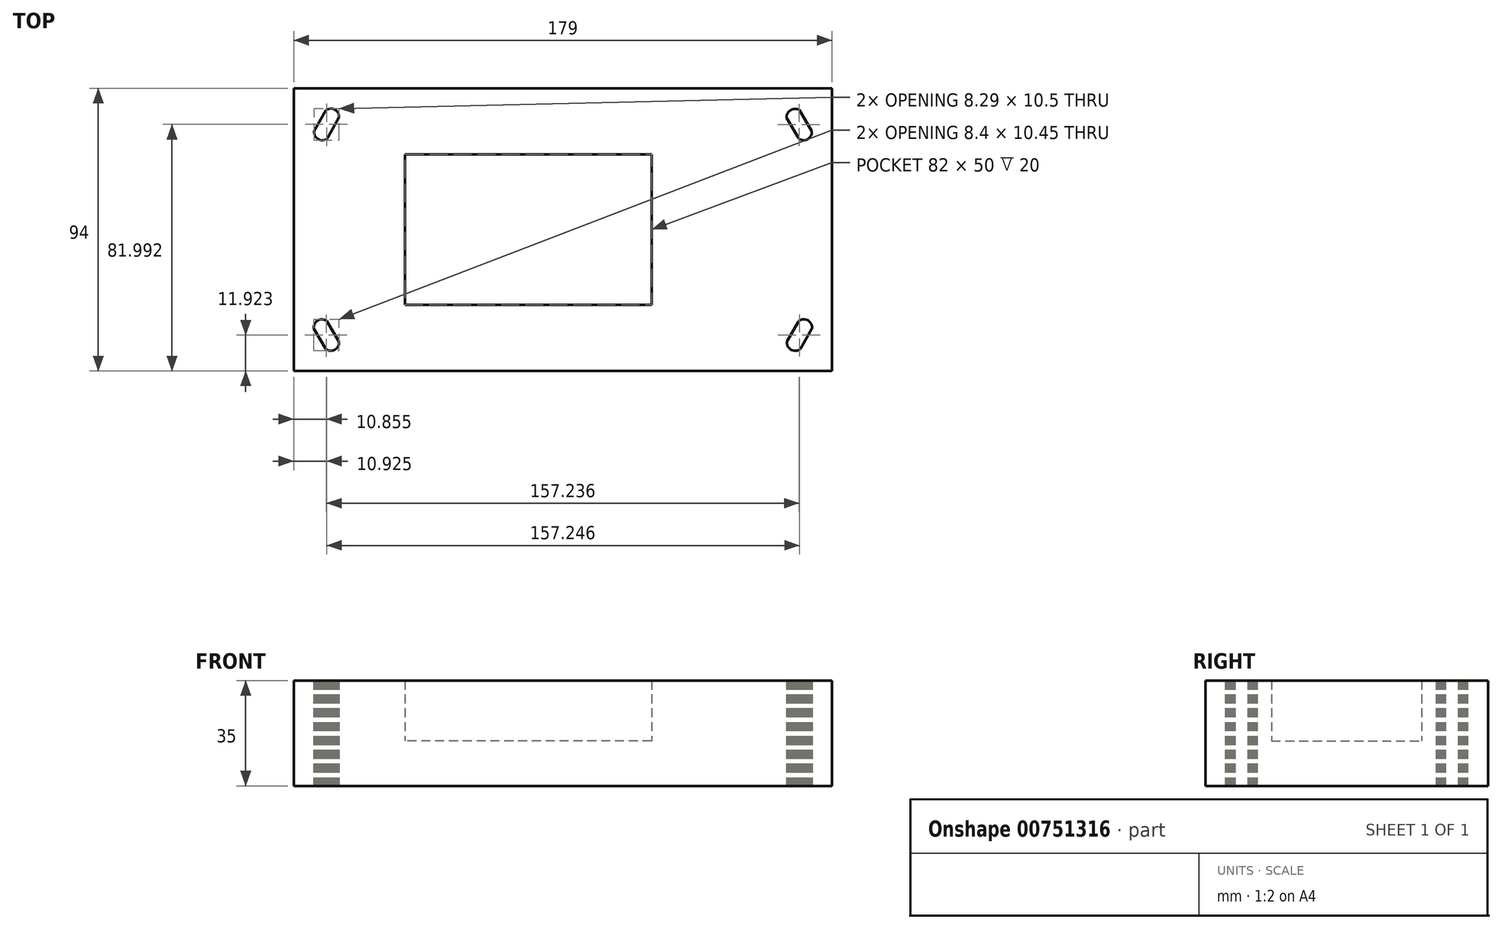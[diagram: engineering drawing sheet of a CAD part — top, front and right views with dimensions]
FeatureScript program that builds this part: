
annotation { "Feature Type Name" : "Feature", "Feature Type Description" : "" }
export const myFeature = defineFeature(function(context is Context, id is Id, definition is map)
    precondition{}
    {
        {
            var Q0;
            Q0=qCreatedBy(makeId("Top.planeOp"),FACE);
            var sketch = newSketch(context, id + "F0", { "sketchPlane" : qUnion([Q0])});
            skLineSegment(sketch, "E0", {"start": v(-79, -30.08) * mm, "end": v(-78.54, -30.33) * mm});
            skLineSegment(sketch, "E1", {"start": v(-79.49, -29.92) * mm, "end": v(-79, -30.08) * mm});
            skLineSegment(sketch, "E2", {"start": v(-80, -29.85) * mm, "end": v(-79.49, -29.92) * mm});
            skLineSegment(sketch, "E3", {"start": v(-80.53, -29.89) * mm, "end": v(-80, -29.85) * mm});
            skLineSegment(sketch, "E4", {"start": v(-81.03, -30.02) * mm, "end": v(-80.53, -29.89) * mm});
            skLineSegment(sketch, "E5", {"start": v(-81.5, -30.24) * mm, "end": v(-81.03, -30.02) * mm});
            skLineSegment(sketch, "E6", {"start": v(-81.92, -30.54) * mm, "end": v(-81.5, -30.24) * mm});
            skLineSegment(sketch, "E7", {"start": v(-82.28, -30.92) * mm, "end": v(-81.92, -30.54) * mm});
            skLineSegment(sketch, "E8", {"start": v(-82.56, -31.36) * mm, "end": v(-82.28, -30.92) * mm});
            skLineSegment(sketch, "E9", {"start": v(-82.75, -31.85) * mm, "end": v(-82.56, -31.36) * mm});
            skLineSegment(sketch, "E10", {"start": v(-82.84, -32.36) * mm, "end": v(-82.75, -31.85) * mm});
            skLineSegment(sketch, "E11", {"start": v(-82.84, -32.88) * mm, "end": v(-82.84, -32.36) * mm});
            skLineSegment(sketch, "E12", {"start": v(-78.77, -39.77) * mm, "end": v(-82.84, -32.88) * mm});
            skLineSegment(sketch, "E13", {"start": v(-78.32, -40.04) * mm, "end": v(-78.77, -39.77) * mm});
            skLineSegment(sketch, "E14", {"start": v(-77.82, -40.22) * mm, "end": v(-78.32, -40.04) * mm});
            skLineSegment(sketch, "E15", {"start": v(-77.3, -40.3) * mm, "end": v(-77.82, -40.22) * mm});
            skLineSegment(sketch, "E16", {"start": v(-76.77, -40.28) * mm, "end": v(-77.3, -40.3) * mm});
            skLineSegment(sketch, "E17", {"start": v(-76.25, -40.15) * mm, "end": v(-76.77, -40.28) * mm});
            skLineSegment(sketch, "E18", {"start": v(-75.77, -39.93) * mm, "end": v(-76.25, -40.15) * mm});
            skLineSegment(sketch, "E19", {"start": v(-75.34, -39.61) * mm, "end": v(-75.77, -39.93) * mm});
            skLineSegment(sketch, "E20", {"start": v(-74.99, -39.22) * mm, "end": v(-75.34, -39.61) * mm});
            skLineSegment(sketch, "E21", {"start": v(-74.71, -38.77) * mm, "end": v(-74.99, -39.22) * mm});
            skLineSegment(sketch, "E22", {"start": v(-74.53, -38.27) * mm, "end": v(-74.71, -38.77) * mm});
            skLineSegment(sketch, "E23", {"start": v(-74.45, -37.75) * mm, "end": v(-74.53, -38.27) * mm});
            skLineSegment(sketch, "E24", {"start": v(78.7, 39.7) * mm, "end": v(82.77, 32.8) * mm});
            skLineSegment(sketch, "E25", {"start": v(78.24, 39.94) * mm, "end": v(78.7, 39.7) * mm});
            skLineSegment(sketch, "E26", {"start": v(77.75, 40.1) * mm, "end": v(78.24, 39.94) * mm});
            skLineSegment(sketch, "E27", {"start": v(77.23, 40.17) * mm, "end": v(77.75, 40.1) * mm});
            skLineSegment(sketch, "E28", {"start": v(76.7, 40.14) * mm, "end": v(77.23, 40.17) * mm});
            skLineSegment(sketch, "E29", {"start": v(76.2, 40) * mm, "end": v(76.7, 40.14) * mm});
            skLineSegment(sketch, "E30", {"start": v(75.73, 39.79) * mm, "end": v(76.2, 40) * mm});
            skLineSegment(sketch, "E31", {"start": v(75.31, 39.48) * mm, "end": v(75.73, 39.79) * mm});
            skLineSegment(sketch, "E32", {"start": v(74.96, 39.1) * mm, "end": v(75.31, 39.48) * mm});
            skLineSegment(sketch, "E33", {"start": v(74.68, 38.66) * mm, "end": v(74.96, 39.1) * mm});
            skLineSegment(sketch, "E34", {"start": v(74.49, 38.18) * mm, "end": v(74.68, 38.66) * mm});
            skLineSegment(sketch, "E35", {"start": v(74.4, 37.67) * mm, "end": v(74.49, 38.18) * mm});
            skLineSegment(sketch, "E36", {"start": v(78.92, 29.99) * mm, "end": v(78.47, 30.26) * mm});
            skLineSegment(sketch, "E37", {"start": v(79.42, 29.8) * mm, "end": v(78.92, 29.99) * mm});
            skLineSegment(sketch, "E38", {"start": v(79.94, 29.73) * mm, "end": v(79.42, 29.8) * mm});
            skLineSegment(sketch, "E39", {"start": v(80.47, 29.75) * mm, "end": v(79.94, 29.73) * mm});
            skLineSegment(sketch, "E40", {"start": v(80.98, 29.88) * mm, "end": v(80.47, 29.75) * mm});
            skLineSegment(sketch, "E41", {"start": v(81.46, 30.1) * mm, "end": v(80.98, 29.88) * mm});
            skLineSegment(sketch, "E42", {"start": v(81.9, 30.41) * mm, "end": v(81.46, 30.1) * mm});
            skLineSegment(sketch, "E43", {"start": v(82.25, 30.8) * mm, "end": v(81.9, 30.41) * mm});
            skLineSegment(sketch, "E44", {"start": v(82.53, 31.25) * mm, "end": v(82.25, 30.8) * mm});
            skLineSegment(sketch, "E45", {"start": v(82.7, 31.75) * mm, "end": v(82.53, 31.25) * mm});
            skLineSegment(sketch, "E46", {"start": v(82.8, 32.28) * mm, "end": v(82.7, 31.75) * mm});
            skLineSegment(sketch, "E47", {"start": v(82.77, 32.8) * mm, "end": v(82.8, 32.28) * mm});
            skLineSegment(sketch, "E48", {"start": v(-74.54, 38.3) * mm, "end": v(-74.44, 37.8) * mm});
            skLineSegment(sketch, "E49", {"start": v(-74.75, 38.79) * mm, "end": v(-74.54, 38.3) * mm});
            skLineSegment(sketch, "E50", {"start": v(-75.03, 39.22) * mm, "end": v(-74.75, 38.79) * mm});
            skLineSegment(sketch, "E51", {"start": v(-75.4, 39.6) * mm, "end": v(-75.03, 39.22) * mm});
            skLineSegment(sketch, "E52", {"start": v(-75.82, 39.9) * mm, "end": v(-75.4, 39.6) * mm});
            skLineSegment(sketch, "E53", {"start": v(-76.3, 40.1) * mm, "end": v(-75.82, 39.9) * mm});
            skLineSegment(sketch, "E54", {"start": v(-76.8, 40.22) * mm, "end": v(-76.3, 40.1) * mm});
            skLineSegment(sketch, "E55", {"start": v(-77.33, 40.24) * mm, "end": v(-76.8, 40.22) * mm});
            skLineSegment(sketch, "E56", {"start": v(-77.84, 40.16) * mm, "end": v(-77.33, 40.24) * mm});
            skLineSegment(sketch, "E57", {"start": v(-78.33, 40) * mm, "end": v(-77.84, 40.16) * mm});
            skLineSegment(sketch, "E58", {"start": v(-78.78, 39.73) * mm, "end": v(-78.33, 40) * mm});
            skLineSegment(sketch, "E59", {"start": v(-82.71, 32.76) * mm, "end": v(-78.78, 39.73) * mm});
            skLineSegment(sketch, "E60", {"start": v(-82.72, 32.23) * mm, "end": v(-82.71, 32.76) * mm});
            skLineSegment(sketch, "E61", {"start": v(-82.63, 31.7) * mm, "end": v(-82.72, 32.23) * mm});
            skLineSegment(sketch, "E62", {"start": v(-82.44, 31.22) * mm, "end": v(-82.63, 31.7) * mm});
            skLineSegment(sketch, "E63", {"start": v(-82.15, 30.77) * mm, "end": v(-82.44, 31.22) * mm});
            skLineSegment(sketch, "E64", {"start": v(-81.78, 30.39) * mm, "end": v(-82.15, 30.77) * mm});
            skLineSegment(sketch, "E65", {"start": v(-81.35, 30.08) * mm, "end": v(-81.78, 30.39) * mm});
            skLineSegment(sketch, "E66", {"start": v(-80.87, 29.87) * mm, "end": v(-81.35, 30.08) * mm});
            skLineSegment(sketch, "E67", {"start": v(-80.35, 29.75) * mm, "end": v(-80.87, 29.87) * mm});
            skLineSegment(sketch, "E68", {"start": v(-79.82, 29.74) * mm, "end": v(-80.35, 29.75) * mm});
            skLineSegment(sketch, "E69", {"start": v(-79.3, 29.83) * mm, "end": v(-79.82, 29.74) * mm});
            skLineSegment(sketch, "E70", {"start": v(-78.8, 30.02) * mm, "end": v(-79.3, 29.83) * mm});
            skLineSegment(sketch, "E71", {"start": v(-78.36, 30.3) * mm, "end": v(-78.8, 30.02) * mm});
            skLineSegment(sketch, "E72", {"start": v(82.82, -32.76) * mm, "end": v(78.9, -39.73) * mm});
            skLineSegment(sketch, "E73", {"start": v(82.8, -32.24) * mm, "end": v(82.82, -32.76) * mm});
            skLineSegment(sketch, "E74", {"start": v(82.7, -31.73) * mm, "end": v(82.8, -32.24) * mm});
            skLineSegment(sketch, "E75", {"start": v(82.5, -31.25) * mm, "end": v(82.7, -31.73) * mm});
            skLineSegment(sketch, "E76", {"start": v(82.21, -30.82) * mm, "end": v(82.5, -31.25) * mm});
            skLineSegment(sketch, "E77", {"start": v(81.85, -30.45) * mm, "end": v(82.21, -30.82) * mm});
            skLineSegment(sketch, "E78", {"start": v(81.42, -30.15) * mm, "end": v(81.85, -30.45) * mm});
            skLineSegment(sketch, "E79", {"start": v(80.95, -29.94) * mm, "end": v(81.42, -30.15) * mm});
            skLineSegment(sketch, "E80", {"start": v(80.44, -29.82) * mm, "end": v(80.95, -29.94) * mm});
            skLineSegment(sketch, "E81", {"start": v(79.92, -29.8) * mm, "end": v(80.44, -29.82) * mm});
            skLineSegment(sketch, "E82", {"start": v(79.4, -29.88) * mm, "end": v(79.92, -29.8) * mm});
            skLineSegment(sketch, "E83", {"start": v(78.91, -30.05) * mm, "end": v(79.4, -29.88) * mm});
            skLineSegment(sketch, "E84", {"start": v(78.46, -30.3) * mm, "end": v(78.91, -30.05) * mm});
            skLineSegment(sketch, "E85", {"start": v(74.62, -38.33) * mm, "end": v(74.52, -37.8) * mm});
            skLineSegment(sketch, "E86", {"start": v(74.81, -38.82) * mm, "end": v(74.62, -38.33) * mm});
            skLineSegment(sketch, "E87", {"start": v(75.1, -39.27) * mm, "end": v(74.81, -38.82) * mm});
            skLineSegment(sketch, "E88", {"start": v(75.46, -39.65) * mm, "end": v(75.1, -39.27) * mm});
            skLineSegment(sketch, "E89", {"start": v(75.9, -39.96) * mm, "end": v(75.46, -39.65) * mm});
            skLineSegment(sketch, "E90", {"start": v(76.38, -40.17) * mm, "end": v(75.9, -39.96) * mm});
            skLineSegment(sketch, "E91", {"start": v(76.9, -40.29) * mm, "end": v(76.38, -40.17) * mm});
            skLineSegment(sketch, "E92", {"start": v(77.43, -40.3) * mm, "end": v(76.9, -40.29) * mm});
            skLineSegment(sketch, "E93", {"start": v(77.95, -40.2) * mm, "end": v(77.43, -40.3) * mm});
            skLineSegment(sketch, "E94", {"start": v(78.44, -40.02) * mm, "end": v(77.95, -40.2) * mm});
            skLineSegment(sketch, "E95", {"start": v(78.9, -39.73) * mm, "end": v(78.44, -40.02) * mm});
            skLineSegment(sketch, "E96", {"start": v(92.5, -50) * mm, "end": v(-92.5, -50) * mm});
            skLineSegment(sketch, "E97", {"start": v(-92.5, -50) * mm, "end": v(-92.5, 50) * mm});
            skLineSegment(sketch, "E98", {"start": v(-92.5, 50) * mm, "end": v(92.5, 50) * mm});
            skLineSegment(sketch, "E99", {"start": v(92.5, 50) * mm, "end": v(92.5, -50) * mm});
            skLineSegment(sketch, "E100", {"start": v(-89.5, -47) * mm, "end": v(-89.5, 47) * mm});
            skLineSegment(sketch, "E101", {"start": v(89.5, -47) * mm, "end": v(-89.5, -47) * mm});
            skLineSegment(sketch, "E102", {"start": v(89.5, 47) * mm, "end": v(89.5, -47) * mm});
            skLineSegment(sketch, "E103", {"start": v(-89.5, 47) * mm, "end": v(89.5, 47) * mm});
            skLineSegment(sketch, "E104", {"start": v(86.7, 46.86) * mm, "end": v(86.74, 46.89) * mm});
            skLineSegment(sketch, "E105", {"start": v(-52.5, -25) * mm, "end": v(-52.5, 25) * mm});
            skLineSegment(sketch, "E106", {"start": v(-52.5, 25) * mm, "end": v(29.5, 25) * mm});
            skLineSegment(sketch, "E107", {"start": v(29.5, 25) * mm, "end": v(29.5, -25) * mm});
            skLineSegment(sketch, "E108", {"start": v(29.5, -25) * mm, "end": v(-52.5, -25) * mm});
            skLineSegment(sketch, "E109", {"start": v(-78.54, -30.33) * mm, "end": v(-78.14, -31.01) * mm});
            skLineSegment(sketch, "E110", {"start": v(-78.14, -31.01) * mm, "end": v(-74.47, -37.22) * mm});
            skLineSegment(sketch, "E111", {"start": v(-74.47, -37.22) * mm, "end": v(-74.45, -37.59) * mm});
            skLineSegment(sketch, "E112", {"start": v(-74.45, -37.59) * mm, "end": v(-74.45, -37.75) * mm});
            skLineSegment(sketch, "E113", {"start": v(74.4, 37.15) * mm, "end": v(74.4, 37.52) * mm});
            skLineSegment(sketch, "E114", {"start": v(74.4, 37.52) * mm, "end": v(74.4, 37.67) * mm});
            skLineSegment(sketch, "E115", {"start": v(78.47, 30.26) * mm, "end": v(78.06, 30.94) * mm});
            skLineSegment(sketch, "E116", {"start": v(78.06, 30.94) * mm, "end": v(74.4, 37.15) * mm});
            skLineSegment(sketch, "E117", {"start": v(-74.43, 37.28) * mm, "end": v(-78.02, 30.9) * mm});
            skLineSegment(sketch, "E118", {"start": v(-78.02, 30.9) * mm, "end": v(-78.36, 30.3) * mm});
            skLineSegment(sketch, "E119", {"start": v(-74.44, 37.8) * mm, "end": v(-74.43, 37.54) * mm});
            skLineSegment(sketch, "E120", {"start": v(-74.43, 37.54) * mm, "end": v(-74.43, 37.28) * mm});
            skLineSegment(sketch, "E121", {"start": v(74.54, -37.28) * mm, "end": v(78.13, -30.9) * mm});
            skLineSegment(sketch, "E122", {"start": v(78.13, -30.9) * mm, "end": v(78.46, -30.3) * mm});
            skLineSegment(sketch, "E123", {"start": v(74.52, -37.8) * mm, "end": v(74.53, -37.54) * mm});
            skLineSegment(sketch, "E124", {"start": v(74.53, -37.54) * mm, "end": v(74.54, -37.28) * mm});
            skSolve(sketch);
        }
        {
            var Q0;
            Q0=makeQuery(id+"F0.imprint","IMPRINT",FACE,{"disambiguationData":[TD([[makeQuery(id+"F0.imprint","IMPRINT",EDGE,{"derivedFrom":sQuery(id+"F0.wireOp",EDGE,"E0")}),1.0]])]});
            extrude(context, id + "F1", {"entities" : qUnion([Q0]), "depth" : 35 * mm, "offsetDistance" : 25 * mm});
        }
        {
            var Q0;
            Q0=makeQuery(id+"F0.imprint","IMPRINT",FACE,{"disambiguationData":[TD([[makeQuery(id+"F0.imprint","IMPRINT",EDGE,{"derivedFrom":sQuery(id+"F0.wireOp",EDGE,"E105")}),-1.0]])]});
            extrude(context, id + "F2", {"entities" : qUnion([Q0]), "operationType" : NewBodyOperationType.ADD, "depth" : 15 * mm, "offsetDistance" : 25 * mm});
        }
    });
